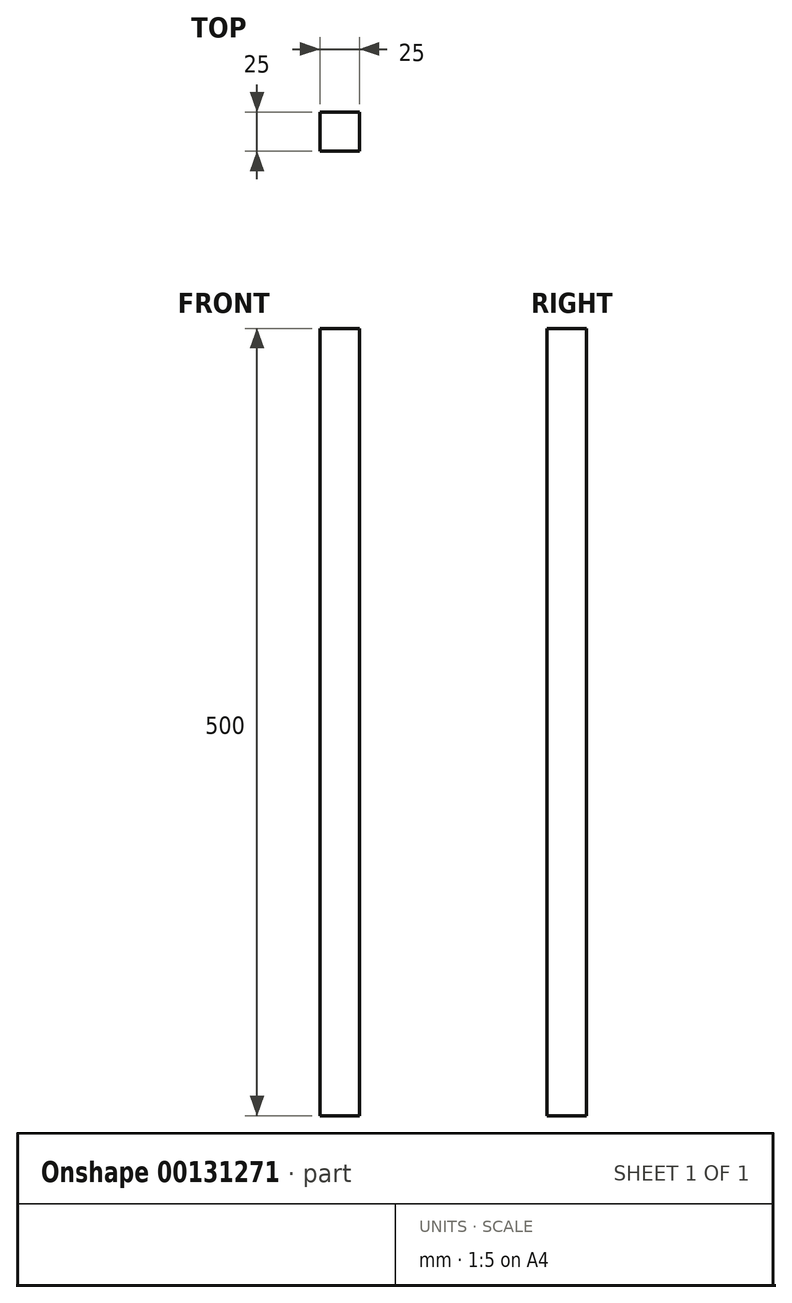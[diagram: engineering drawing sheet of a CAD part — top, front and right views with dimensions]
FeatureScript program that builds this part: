
annotation { "Feature Type Name" : "Feature", "Feature Type Description" : "" }
export const myFeature = defineFeature(function(context is Context, id is Id, definition is map)
    precondition{}
    {
        {
            var Q0;
            Q0=qCreatedBy(makeId("Top.planeOp"),FACE);
            var sketch = newSketch(context, id + "F0", { "sketchPlane" : qUnion([Q0])});
            skLineSegment(sketch, "E0.bottom", {"start": v(0, 0) * mm, "end": v(25, 0) * mm});
            skLineSegment(sketch, "E0.top", {"start": v(0, 25) * mm, "end": v(25, 25) * mm});
            skLineSegment(sketch, "E0.left", {"start": v(0, 0) * mm, "end": v(0, 25) * mm});
            skLineSegment(sketch, "E0.right", {"start": v(25, 0) * mm, "end": v(25, 25) * mm});
            skSolve(sketch);
        }
        {
            var Q0;
            Q0 = qSketchRegion(id + "F0", true);
            extrude(context, id + "F1", {"entities" : qUnion([Q0]), "depth" : 500 * mm});
        }
    });
